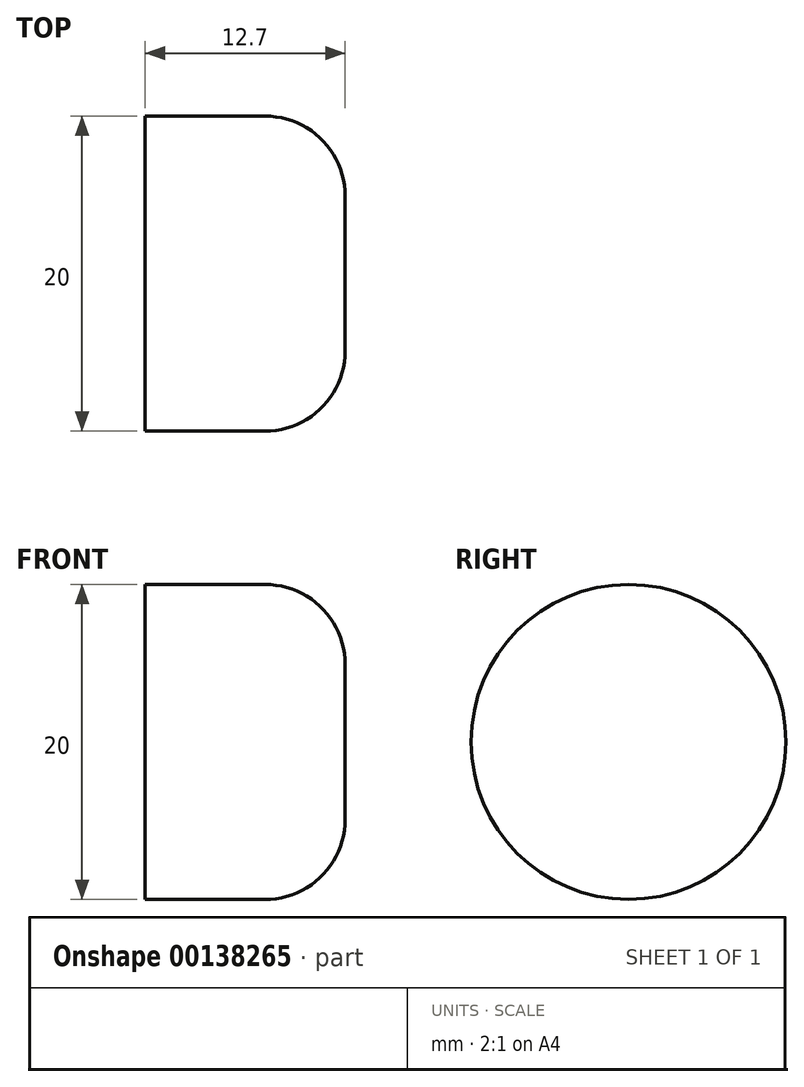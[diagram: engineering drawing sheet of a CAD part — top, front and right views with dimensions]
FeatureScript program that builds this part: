
annotation { "Feature Type Name" : "Feature", "Feature Type Description" : "" }
export const myFeature = defineFeature(function(context is Context, id is Id, definition is map)
    precondition{}
    {
        {
            var Q0;
            Q0=qCreatedBy(makeId("Right.planeOp"),FACE);
            var sketch = newSketch(context, id + "F0", { "sketchPlane" : qUnion([Q0])});
            skCircle(sketch, "E0", {"center": v(0, 0) * mm, "radius": 10 * mm});
            skSolve(sketch);
        }
        {
            var Q0;
            Q0=makeQuery(id+"F0.imprint","IMPRINT",FACE,{"disambiguationData":[TD([[makeQuery(id+"F0.imprint","IMPRINT",EDGE,{"derivedFrom":sQuery(id+"F0.wireOp",EDGE,"E0")}),1.0]])]});
            extrude(context, id + "F1", {"entities" : qUnion([Q0]), "depth" : 12.7 * mm});
        }
        {
            var Q0;
            Q0=makeQuery(id+"F1.opExtrude","CAP_EDGE",EDGE,{"disambiguationData":[OSD([sQuery(id+"F0.wireOp",EDGE,"E0")])],"isStart":false});
            fillet(context, id + "F2", {"entities" : qUnion([Q0]), "radius" : 5.08 * mm, "tangentPropagation" : true, "allowEdgeOverflow" : false});
        }
    });
